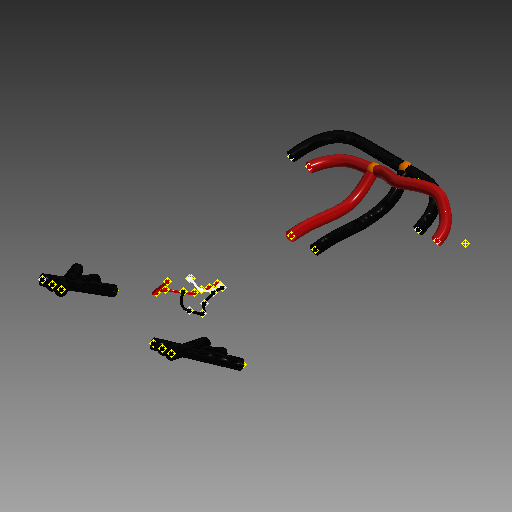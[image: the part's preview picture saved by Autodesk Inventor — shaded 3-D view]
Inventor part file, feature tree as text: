
AUTODESK INVENTOR PART (.ipt)
format: ipt  version: 2019.2 (Build 232265000, 265)  size: 1,439,744 bytes
history: native  units: mm (DEFAULTED — no unit token found)
features: other x108, sketch x29, plane x27, sweep x27, revolve x2
ambient origin geometry x8: Origin, YZ Plane, XZ Plane, XY Plane, X Axis, Y Axis, Z Axis, Center Point
bodies: Body1 (feature_tree), Body2 (feature_tree), Body3 (feature_tree), Body4 (feature_tree), Body5 (feature_tree), Body6 (feature_tree), Body7 (feature_tree), Body8 (feature_tree), Body9 (feature_tree), Body10 (feature_tree), Body11 (feature_tree), Body12 (feature_tree), Body13 (feature_tree), Body14 (feature_tree), Body15 (feature_tree), Body16 (feature_tree), Body17 (feature_tree), Body18 (feature_tree), Body19 (feature_tree), Body20 (feature_tree), Body21 (feature_tree), Body22 (feature_tree), Body23 (feature_tree), Body24 (feature_tree), Body25 (feature_tree), Body26 (feature_tree), Body27 (feature_tree), Body28 (feature_tree), Body29 (feature_tree)
feature tree (193):
  other  "Work Point3"
  other  "Work Point4"
  other  "n_vesc"
  other  "Work Point12"
  other  "Work Point13"
  other  "p_vesc"
  other  "Work Point20"
  other  "Work Point21"
  other  "n_out"
  other  "Work Point28"
  other  "Work Point29"
  other  "p_out"
  other  "Work Point30"
  other  "Work Point37"
  other  "Work Point38"
  other  "m1_3"
  other  "Work Point39"
  other  "Work Point40"
  other  "m1_2"
  other  "Work Point41"
  other  "Work Point42"
  other  "m1_1"
  other  "Work Point43"
  other  "Work Point44"
  other  "m2_3"
  other  "Work Point45"
  other  "Work Point46"
  other  "m2_2"
  other  "Work Point47"
  other  "Work Point48"
  other  "m2_1"
  plane  "Work Plane21"
  plane  "Work Plane22"
  plane  "Work Plane23"
  plane  "Work Plane24"
  plane  "Work Plane25"
  plane  "Work Plane26"
  other  "Work Point49"
  other  "Segment1"
  other  "Work Point51"
  plane  "Work Plane37"
  plane  "Work Plane38"
  other  "Work Point52"
  other  "Work Point53"
  other  "Segment2"
  other  "Work Point54"
  other  "Work Point55"
  other  "Work Point56"
  plane  "Work Plane40"
  plane  "Work Plane41"
  other  "Work Point58"
  other  "Work Point59"
  other  "Work Point60"
  other  "Segment2_1"
  plane  "Work Plane42"
  plane  "Work Plane43"
  other  "Work Point61"
  other  "Segment3"
  other  "Work Point62"
  plane  "Work Plane44"
  plane  "Work Plane45"
  other  "Work Point63"
  other  "Work Point65"
  other  "Work Point66"
  other  "Work Point67"
  other  "Segment1_1"
  plane  "Work Plane46"
  plane  "Work Plane47"
  other  "Work Point68"
  other  "Segment4"
  other  "Work Point69"
  plane  "Work Plane48"
  other  "Work Point70"
  plane  "Work Plane49"
  other  "Work Point77"
  other  "Work Point78"
  other  "Segment5"
  other  "Work Point79"
  other  "Work Point80"
  plane  "Work Plane53"
  other  "Work Point81"
  other  "Work Point82"
  other  "Segment6"
  other  "Work Point83"
  other  "Work Point84"
  plane  "Work Plane56"
  other  "Work Point85"
  other  "Work Point86"
  other  "Segment7"
  other  "Work Point87"
  plane  "Work Plane59"
  other  "Work Point88"
  other  "Work Point89"
  other  "Wire1"
  other  "Work Point90"
  other  "Work Point91"
  other  "Wire2"
  other  "Work Point92"
  other  "Work Point93"
  other  "Wire3"
  plane  "Work Plane62"
  plane  "Work Plane63"
  plane  "Work Plane64"
  plane  "Work Plane65"
  plane  "Work Plane66"
  plane  "Work Plane67"
  sketch  "Sketch23"  dims[d38=0.0mm d39=0.0mm d40=0.0mm d41=0.0mm]
  other  "Srf21"
  sketch  "Sketch24"  dims[d42=0.0mm d43=0.0mm d44=0.0mm d45=0.0mm]
  other  "Srf22"
  sketch  "Sketch25"  dims[d46=0.0mm d47=0.0mm d48=0.0mm d49=0.0mm]
  other  "Srf23"
  sketch  "Sketch26"  dims[d68=0.0mm d69=0.0mm d70=0.0mm d71=0.0mm]
  other  "Srf24"
  sketch  "Sketch27"  dims[d74=0.0mm d75=0.0mm d76=0.0mm d77=0.0mm]
  other  "Srf25"
  sketch  "Sketch28"  dims[d78=0.0mm d79=0.0mm d80=0.0mm d81=0.0mm]
  other  "Srf26"
  sketch  "Sketch39"  dims[d82=0.0mm d83=0.0mm d84=0.0mm]
  other  "Srf36"
  sketch  "Sketch40"  dims[d85=0.0mm d86=0.0mm d87=0.0mm d88=0.0mm]
  other  "Srf37"
  sketch  "Sketch42"  dims[d89=0.0mm d90=0.0mm d91=0.0mm]
  other  "Srf39"
  sketch  "Sketch43"  dims[d92=0.0mm d93=0.0mm d94=0.0mm d95=0.0mm]
  other  "Srf40"
  sketch  "Sketch44"  dims[d102=0.0mm d103=0.0mm d108=0.0mm d109=0.0mm]
  other  "Srf41"
  sketch  "Sketch45"  dims[d114=0.0mm d115=0.0mm d120=0.0mm d121=0.0mm]
  other  "Srf42"
  sketch  "Sketch46"  dims[d122=0.0mm d123=0.0mm d124=0.0mm d125=0.0mm]
  other  "Srf43"
  sketch  "Sketch47"  dims[d126=0.0mm d127=0.0mm d128=0.0mm d129=0.0mm]
  other  "Srf44"
  sketch  "Sketch48"  dims[d130=0.0mm d131=0.0mm]
  other  "Srf45"
  sketch  "Sketch49"
  other  "Srf46"
  sketch  "Sketch50"
  other  "Srf47"
  sketch  "Sketch51"
  other  "Srf48"
  sketch  "Sketch52"
  other  "Srf49"
  sketch  "Sketch53"
  other  "Srf50"
  sketch  "Sketch57"
  other  "Srf54"
  sketch  "Sketch60"
  other  "Srf57"
  sketch  "Sketch63"
  other  "Srf60"
  sketch  "Sketch66"
  other  "Srf63"
  sketch  "Sketch67"
  other  "Srf64"
  sketch  "Sketch68"
  other  "Srf65"
  sketch  "Sketch69"
  other  "Srf66"
  sketch  "Sketch70"
  other  "Srf67"
  sketch  "Sketch71"
  other  "Srf68"
  sweep  "SweepSrf19"
  sweep  "SweepSrf20"
  sweep  "SweepSrf21"
  sweep  "SweepSrf22"
  sweep  "SweepSrf23"
  sweep  "SweepSrf24"
  sweep  "SweepSrf34"
  sweep  "SweepSrf35"
  sweep  "SweepSrf37"
  sweep  "SweepSrf38"
  sweep  "SweepSrf39"
  sweep  "SweepSrf40"
  revolve  "RevolutionSrf3"  [1 undecoded]
  sweep  "SweepSrf41"
  sweep  "SweepSrf42"
  sweep  "SweepSrf43"
  sweep  "SweepSrf44"
  revolve  "RevolutionSrf4"  [1 undecoded]
  sweep  "SweepSrf45"
  sweep  "SweepSrf46"
  sweep  "SweepSrf50"
  sweep  "SweepSrf53"
  sweep  "SweepSrf56"
  sweep  "SweepSrf59"
  sweep  "SweepSrf60"
  sweep  "SweepSrf61"
  sweep  "SweepSrf62"
  sweep  "SweepSrf63"
  sweep  "SweepSrf64"
note: 2 required parameter values undecoded (feature->parameter linkage not recoverable at this tier; creation-order binding heuristic only, values carry confidence <= 0.55)